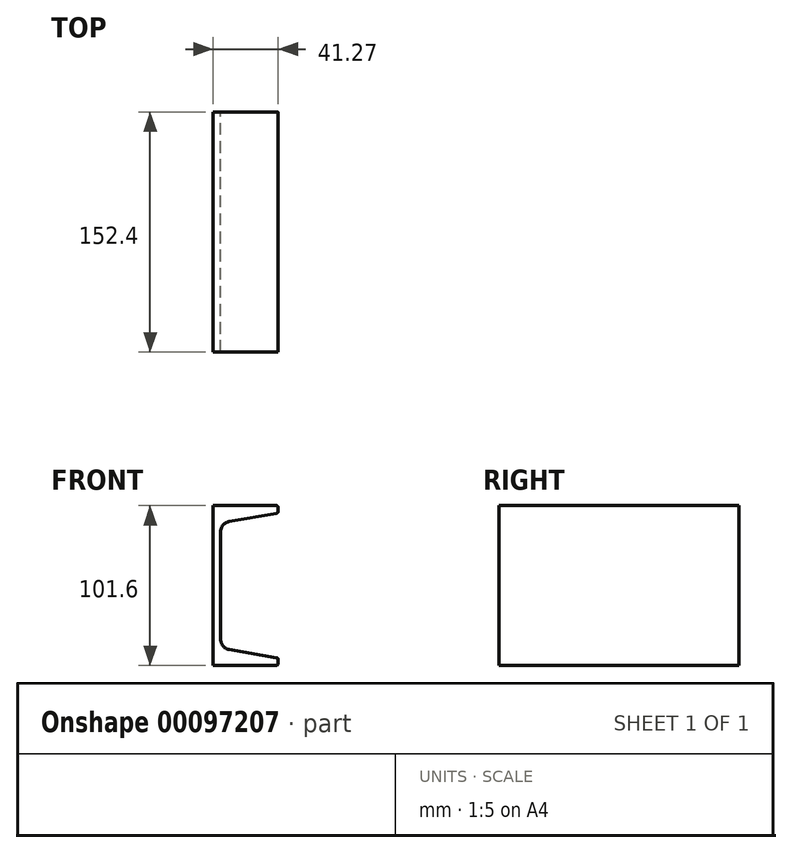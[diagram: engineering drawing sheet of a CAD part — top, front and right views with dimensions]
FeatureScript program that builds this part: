
annotation { "Feature Type Name" : "Feature", "Feature Type Description" : "" }
export const myFeature = defineFeature(function(context is Context, id is Id, definition is map)
    precondition{}
    {
        {
            var Q0;
            Q0=qCreatedBy(makeId("Front.planeOp"),FACE);
            var sketch = newSketch(context, id + "F0", { "sketchPlane" : qUnion([Q0])});
            skLineSegment(sketch, "E0", {"start": v(0, 0) * mm, "end": v(0, 101.6) * mm});
            skLineSegment(sketch, "E1", {"start": v(0, 101.6) * mm, "end": v(40, 101.6) * mm});
            skLineSegment(sketch, "E2", {"start": v(41.28, 100.33) * mm, "end": v(41.28, 97.9) * mm});
            skLineSegment(sketch, "E3", {"start": v(40.22, 96.65) * mm, "end": v(10.02, 91.4) * mm});
            skLineSegment(sketch, "E4", {"start": v(4.76, 85.15) * mm, "end": v(4.76, 16.45) * mm});
            skLineSegment(sketch, "E5", {"start": v(0, 0) * mm, "end": v(40, 0) * mm});
            skLineSegment(sketch, "E6", {"start": v(41.28, 1.27) * mm, "end": v(41.28, 3.7) * mm});
            skLineSegment(sketch, "E7", {"start": v(40.22, 4.95) * mm, "end": v(10.02, 10.2) * mm});
            skPoint(sketch, "E8.visualSharp", {"position": v(41.28, 101.6) * mm});
            skArc(sketch, "E8.filletArc", {"start": v(41.28, 100.33) * mm, "mid": v(40.9, 101.23) * mm, "end": v(40, 101.6) * mm});
            skPoint(sketch, "E9.visualSharp", {"position": v(41.28, 96.84) * mm});
            skArc(sketch, "E9.filletArc", {"start": v(40.22, 96.65) * mm, "mid": v(40.98, 97.09) * mm, "end": v(41.28, 97.9) * mm});
            skPoint(sketch, "E10.visualSharp", {"position": v(41.28, 4.76) * mm});
            skArc(sketch, "E10.filletArc", {"start": v(41.28, 3.7) * mm, "mid": v(40.98, 4.51) * mm, "end": v(40.22, 4.95) * mm});
            skPoint(sketch, "E11.visualSharp", {"position": v(41.28, 0) * mm});
            skArc(sketch, "E11.filletArc", {"start": v(40, 0) * mm, "mid": v(40.9, 0.37) * mm, "end": v(41.28, 1.27) * mm});
            skPoint(sketch, "E12.visualSharp", {"position": v(4.76, 90.49) * mm});
            skArc(sketch, "E12.filletArc", {"start": v(10.02, 91.4) * mm, "mid": v(6.25, 89.23) * mm, "end": v(4.76, 85.15) * mm});
            skPoint(sketch, "E13.visualSharp", {"position": v(4.76, 11.11) * mm});
            skArc(sketch, "E13.filletArc", {"start": v(4.76, 16.45) * mm, "mid": v(6.25, 12.37) * mm, "end": v(10.02, 10.2) * mm});
            skSolve(sketch);
        }
        {
            var Q0;
            Q0=makeQuery(id+"F0.imprint","IMPRINT",FACE,{"disambiguationData":[TD([[makeQuery(id+"F0.imprint","IMPRINT",EDGE,{"derivedFrom":sQuery(id+"F0.wireOp",EDGE,"E0")}),-1.0]])]});
            extrude(context, id + "F1", {"entities" : qUnion([Q0]), "depth" : 152.4 * mm});
        }
    });
